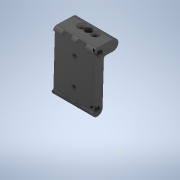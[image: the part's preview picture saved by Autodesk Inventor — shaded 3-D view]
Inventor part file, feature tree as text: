
AUTODESK INVENTOR PART (.ipt)
format: ipt  version: 2020 (Build 240168000, 168)  size: 340,480 bytes
history: native  units: in
note: dims shown in document units (in); Inventor stores cm internally (conversion verified against a paired STEP export)
features: extrude x6, sketch x6, projected_geometry x2
ambient origin geometry x8: Origin, YZ Plane, XZ Plane, XY Plane, X Axis, Y Axis, Z Axis, Center Point
bodies: Solid2 (feature_tree), Solid1 (feature_tree)
feature tree (14):
  extrude  "Extrusion1"  Depth=0.126in
  extrude  "add 5mm left"  Depth=0.1969in TaperAngle=0.0deg
  extrude  "add 5mm right"  Depth=0.1181in
  extrude  "fin mount holes"  Depth=0.3937in TaperAngle=0.0deg
  extrude  "add standoff holes"  Depth=0.2008in
  extrude  "add nuts for mounting"  Depth=0.2205in
  sketch  "Sketch1"  dims[d0=0.126in d1=0.126in]
  sketch  "Sketch2"  dims[d2=0.3937in d3=0.0in d4=0.1969in d5=0.0in]
  projected_geometry  "Projected Loop1"
  sketch  "Sketch3"  dims[d6=0.1969in d7=0.0in d8=0.1181in]
  projected_geometry  "Projected Loop2"
  sketch  "Sketch4"  dims[d9=0.1181in d10=0.3937in d11=0.0in]
  sketch  "Sketch5"  dims[d12=0.2008in d13=0.2008in]
  sketch  "Sketch6"  dims[d14=0.3937in d15=0.0in d16=0.2205in d17=0.2205in d18=0.0984in d19=0.0in]
